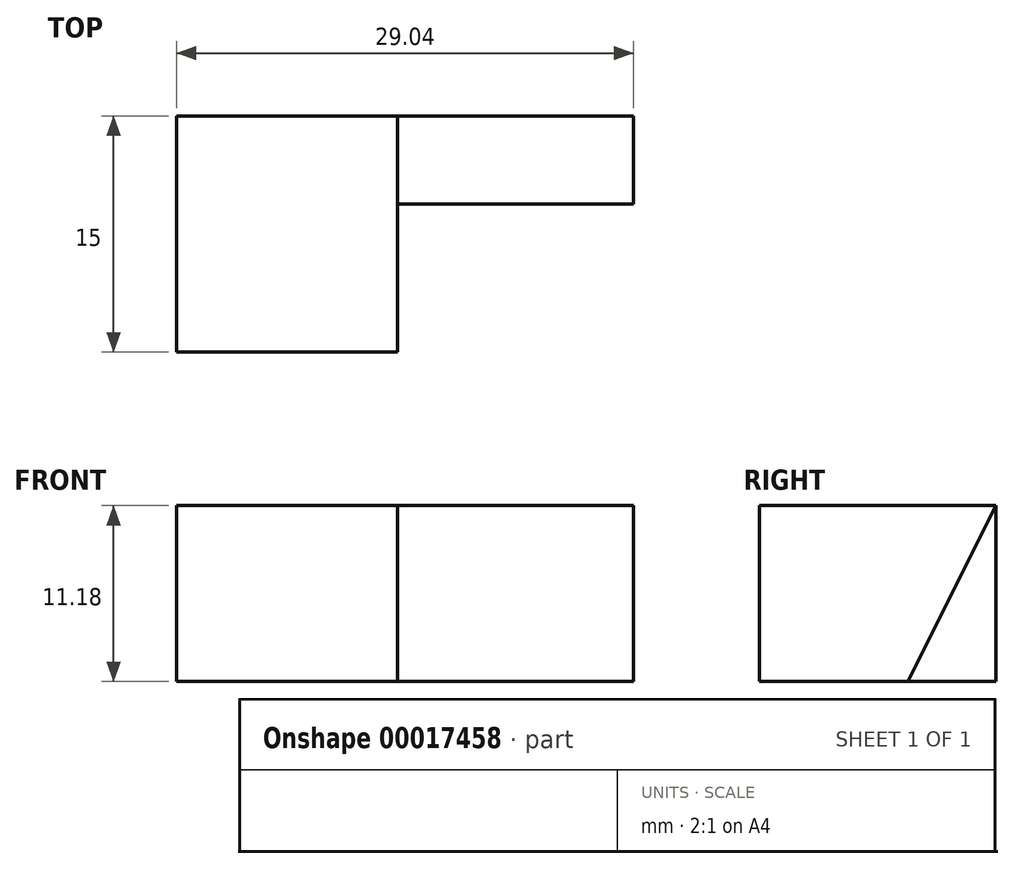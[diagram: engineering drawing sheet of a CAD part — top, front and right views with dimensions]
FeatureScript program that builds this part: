
annotation { "Feature Type Name" : "Feature", "Feature Type Description" : "" }
export const myFeature = defineFeature(function(context is Context, id is Id, definition is map)
    precondition{}
    {
        {
            var Q0;
            Q0=qCreatedBy(makeId("Front.planeOp"),FACE);
            var sketch = newSketch(context, id + "F0", { "sketchPlane" : qUnion([Q0])});
            skLineSegment(sketch, "E0.rect.bottom", {"start": v(-14.52, -13.09) * mm, "end": v(14.52, -13.09) * mm});
            skLineSegment(sketch, "E0.rect.top", {"start": v(-14.52, 13.09) * mm, "end": v(14.52, 13.09) * mm});
            skLineSegment(sketch, "E0.rect.left", {"start": v(-14.52, -13.09) * mm, "end": v(-14.52, 13.09) * mm});
            skLineSegment(sketch, "E0.rect.right", {"start": v(14.52, -13.09) * mm, "end": v(14.52, 13.09) * mm});
            skPoint(sketch, "E0.rect.middle", {"position": v(0, 0) * mm});
            skSolve(sketch);
        }
        {
            var Q0;
            Q0=makeQuery(id+"F0.imprint","IMPRINT",FACE,{"disambiguationData":[TD([[makeQuery(id+"F0.imprint","IMPRINT",EDGE,{"derivedFrom":sQuery(id+"F0.wireOp",EDGE,"E0.rect.bottom")}),1.0]])]});
            extrude(context, id + "F1", {"entities" : qUnion([Q0]), "depth" : 15 * mm});
        }
        {
            var Q0;
            Q0=makeQuery(id+"F1.opExtrude","SWEPT_FACE",FACE,{"disambiguationData":[OSD([sQuery(id+"F0.wireOp",EDGE,"E0.rect.right")])]});
            extrude(context, id + "F2", {"entities" : qUnion([Q0]), "operationType" : NewBodyOperationType.REMOVE, "oppositeDirection" : true, "depth" : 15 * mm});
        }
        {
            var Q0;
            Q0=makeQuery(id+"F1.opExtrude","SWEPT_FACE",FACE,{"disambiguationData":[OSD([sQuery(id+"F0.wireOp",EDGE,"E0.rect.top")])]});
            extrude(context, id + "F3", {"entities" : qUnion([Q0]), "operationType" : NewBodyOperationType.REMOVE, "oppositeDirection" : true, "depth" : 15 * mm});
        }
        {
            var Q0;
            Q0=makeQuery(id+"F2.boolean.opBoolean","COPY",FACE,{"derivedFrom":makeQuery(id+"F2.opExtrude","CAP_FACE",FACE,{"disambiguationData":[OSD([sQuery(id+"F0.wireOp",EDGE,"E0.rect.right")])],"isStart":false})});
            var sketch = newSketch(context, id + "F4", { "sketchPlane" : qUnion([Q0])});
            skLineSegment(sketch, "E1", {"start": v(-5.6, -13.09) * mm, "end": v(0, -1.91) * mm});
            skLineSegment(sketch, "E2", {"start": v(-5.6, -13.09) * mm, "end": v(0, -13.09) * mm});
            skLineSegment(sketch, "E3", {"start": v(0, -13.09) * mm, "end": v(0, -1.91) * mm});
            skSolve(sketch);
        }
        {
            var Q0;
            Q0=makeQuery(id+"F4.imprint","IMPRINT",FACE,{"disambiguationData":[TD([[makeQuery(id+"F4.imprint","IMPRINT",EDGE,{"derivedFrom":sQuery(id+"F4.wireOp",EDGE,"E1")}),-1.0]])]});
            extrude(context, id + "F5", {"entities" : qUnion([Q0]), "operationType" : NewBodyOperationType.ADD, "depth" : 15 * mm});
        }
    });
